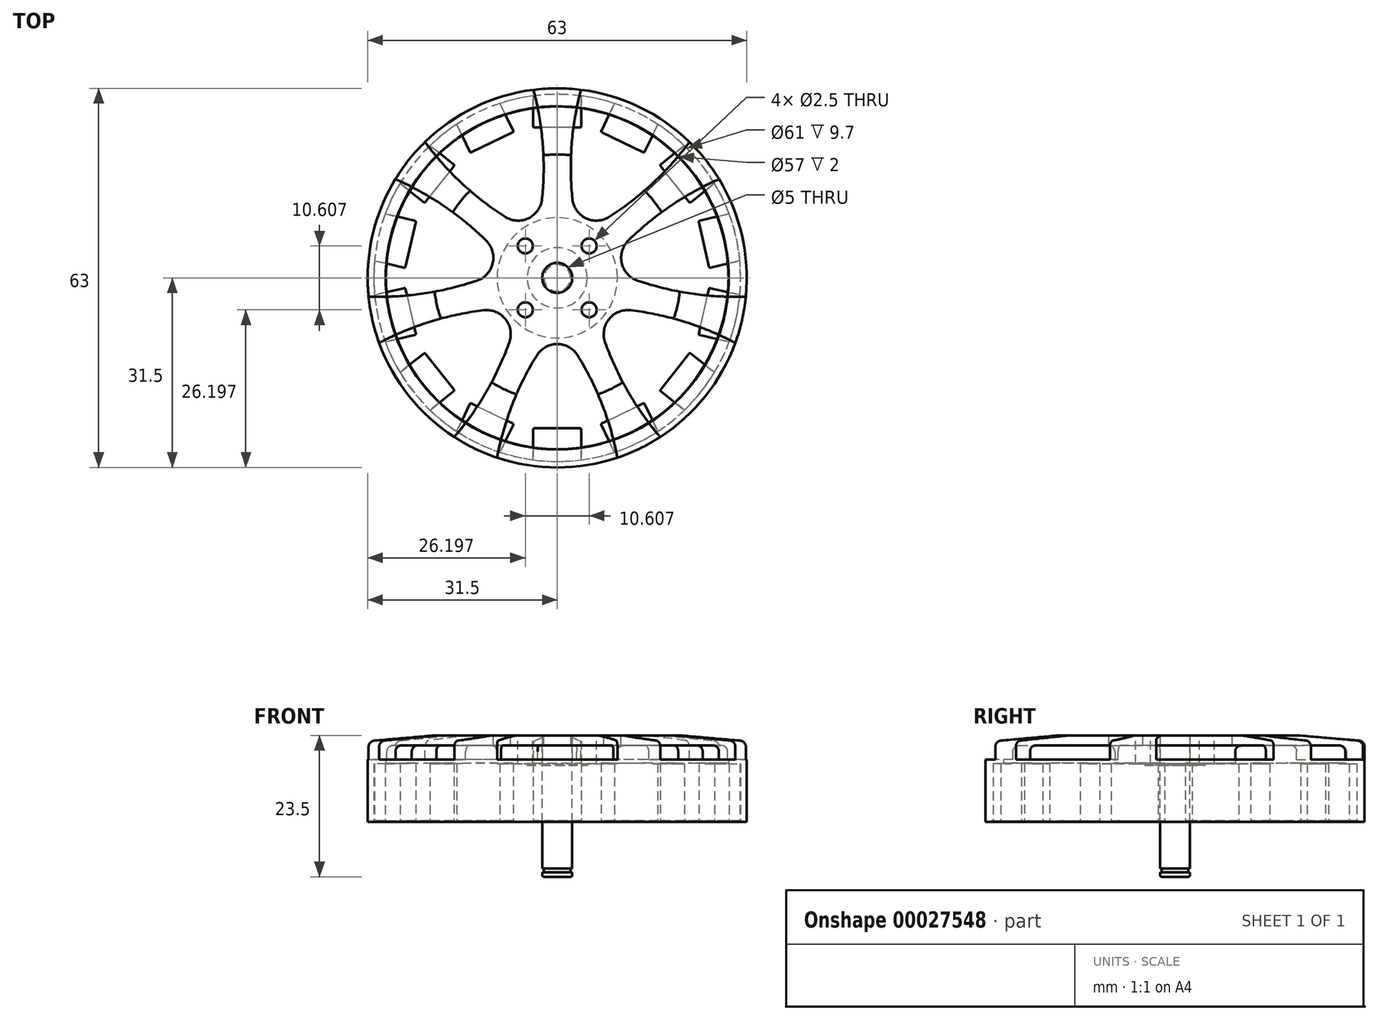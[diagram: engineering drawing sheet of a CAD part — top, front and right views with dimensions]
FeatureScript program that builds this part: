
annotation { "Feature Type Name" : "Feature", "Feature Type Description" : "" }
export const myFeature = defineFeature(function(context is Context, id is Id, definition is map)
    precondition{}
    {
        {
            var Q0;
            Q0=qCreatedBy(makeId("Front.planeOp"),FACE);
            var sketch = newSketch(context, id + "F0", { "sketchPlane" : qUnion([Q0])});
            skLineSegment(sketch, "E0", {"start": v(-2.5, 14.4) * mm, "end": v(-20.5, 14.4) * mm});
            skLineSegment(sketch, "E1", {"start": v(-20.5, 14.4) * mm, "end": v(-30.59, 13.52) * mm});
            skLineSegment(sketch, "E2", {"start": v(-31.5, 12.52) * mm, "end": v(-31.5, 0) * mm});
            skLineSegment(sketch, "E3", {"start": v(-31.5, 0) * mm, "end": v(-30.5, 0) * mm});
            skLineSegment(sketch, "E4", {"start": v(-30.5, 0) * mm, "end": v(-30.5, 9.7) * mm});
            skLineSegment(sketch, "E5", {"start": v(-10, 11.7) * mm, "end": v(-10, 9.7) * mm});
            skLineSegment(sketch, "E6", {"start": v(-10, 9.7) * mm, "end": v(-5, 9.7) * mm});
            skLineSegment(sketch, "E7", {"start": v(-2.5, 14.4) * mm, "end": v(-2.5, 9.7) * mm});
            skLineSegment(sketch, "E8", {"start": v(-30.5, 9.7) * mm, "end": v(-28.5, 9.7) * mm});
            skLineSegment(sketch, "E9", {"start": v(-28.5, 9.7) * mm, "end": v(-28.5, 11.7) * mm});
            skLineSegment(sketch, "E10", {"start": v(-27.5, 12.7) * mm, "end": v(-11, 12.7) * mm});
            skPoint(sketch, "E11.visualSharp", {"position": v(-28.5, 12.7) * mm});
            skArc(sketch, "E11.filletArc", {"start": v(-27.5, 12.7) * mm, "mid": v(-28.2, 12.4) * mm, "end": v(-28.5, 11.7) * mm});
            skPoint(sketch, "E12.visualSharp", {"position": v(-31.5, 13.44) * mm});
            skArc(sketch, "E12.filletArc", {"start": v(-30.59, 13.52) * mm, "mid": v(-31.24, 13.2) * mm, "end": v(-31.5, 12.52) * mm});
            skPoint(sketch, "E13.visualSharp", {"position": v(-10, 12.7) * mm});
            skArc(sketch, "E13.filletArc", {"start": v(-10, 11.7) * mm, "mid": v(-10.3, 12.4) * mm, "end": v(-11, 12.7) * mm});
            skLineSegment(sketch, "E14", {"start": v(0, 0) * mm, "end": v(0, 25.5) * mm, "construction": true});
            skLineSegment(sketch, "E15", {"start": v(-5, 9.7) * mm, "end": v(-5, 9.4) * mm});
            skLineSegment(sketch, "E16", {"start": v(-5, 9.4) * mm, "end": v(-2.5, 9.4) * mm});
            skLineSegment(sketch, "E17", {"start": v(-2.5, 9.4) * mm, "end": v(-2.5, 9.7) * mm});
            skSolve(sketch);
        }
        {
            var Q0;
            Q0=makeQuery(id+"F0.imprint","IMPRINT",FACE,{"disambiguationData":[TD([[makeQuery(id+"F0.imprint","IMPRINT",EDGE,{"derivedFrom":sQuery(id+"F0.wireOp",EDGE,"E0")}),1.0]])]});
            var Q1;
            Q1=sQuery(id+"F0.wireOp",EDGE,"E14");
            revolve(context, id + "F1", {"entities" : qUnion([Q0]), "axis" : qUnion([Q1]), "revolveType" : RevolveType.FULL});
        }
        {
            var Q0;
            Q0=makeQuery(id+"F1.opRevolve","SWEPT_FACE",FACE,{"disambiguationData":[OSD([sQuery(id+"F0.wireOp",EDGE,"E0")])]});
            var sketch = newSketch(context, id + "F2", { "sketchPlane" : qUnion([Q0])});
            skArc(sketch, "E18", {"start": v(0, -11) * mm, "mid": v(-1.95, -11.5) * mm, "end": v(-3.4, -12.9) * mm});
            skArc(sketch, "E19.0", {"start": v(-10, -29.87) * mm, "mid": v(-5.07, -31.09) * mm, "end": v(0, -31.5) * mm});
            skArc(sketch, "E20", {"start": v(-3.4, -12.9) * mm, "mid": v(-7.48, -21.08) * mm, "end": v(-10, -29.87) * mm});
            skLineSegment(sketch, "E21", {"start": v(0, 0) * mm, "end": v(0, -34.41) * mm, "construction": true});
            skPoint(sketch, "E22", {"position": v(0, -11) * mm});
            skPoint(sketch, "E23", {"position": v(0, -31.5) * mm});
            skArc(sketch, "E24.MirrorCS", {"start": v(0, -11) * mm, "mid": v(1.95, -11.5) * mm, "end": v(3.4, -12.9) * mm});
            skArc(sketch, "E25.MirrorCS", {"start": v(10, -29.87) * mm, "mid": v(5.07, -31.09) * mm, "end": v(0, -31.5) * mm});
            skArc(sketch, "E26.MirrorCS", {"start": v(3.4, -12.9) * mm, "mid": v(7.48, -21.08) * mm, "end": v(10, -29.87) * mm});
            skPoint(sketch, "E27.1.0", {"position": v(24.63, -19.64) * mm});
            skPoint(sketch, "E27.1.1", {"position": v(8.6, -6.86) * mm});
            skArc(sketch, "E27.1.2", {"start": v(17.12, -26.44) * mm, "mid": v(21.15, -23.34) * mm, "end": v(24.63, -19.64) * mm});
            skArc(sketch, "E27.1.3", {"start": v(7.96, -10.7) * mm, "mid": v(11.82, -19) * mm, "end": v(17.12, -26.44) * mm});
            skArc(sketch, "E27.1.4", {"start": v(29.59, -10.8) * mm, "mid": v(27.47, -15.42) * mm, "end": v(24.63, -19.64) * mm});
            skArc(sketch, "E27.1.5", {"start": v(12.2, -5.38) * mm, "mid": v(21.15, -7.3) * mm, "end": v(29.59, -10.8) * mm});
            skPoint(sketch, "E27.1.6", {"position": v(24.63, -19.64) * mm});
            skPoint(sketch, "E27.1.7", {"position": v(8.6, -6.86) * mm});
            skArc(sketch, "E27.1.8", {"start": v(8.6, -6.86) * mm, "mid": v(7.78, -8.7) * mm, "end": v(7.96, -10.7) * mm});
            skArc(sketch, "E27.1.9", {"start": v(8.6, -6.86) * mm, "mid": v(10.2, -5.65) * mm, "end": v(12.2, -5.38) * mm});
            skPoint(sketch, "E27.2.0", {"position": v(30.71, 7) * mm});
            skPoint(sketch, "E27.2.1", {"position": v(10.72, 2.45) * mm});
            skArc(sketch, "E27.2.2", {"start": v(31.35, -3.1) * mm, "mid": v(31.44, 1.98) * mm, "end": v(30.71, 7) * mm});
            skArc(sketch, "E27.2.3", {"start": v(13.33, -0.45) * mm, "mid": v(22.22, -2.6) * mm, "end": v(31.35, -3.1) * mm});
            skArc(sketch, "E27.2.4", {"start": v(26.9, 16.4) * mm, "mid": v(29.18, 11.86) * mm, "end": v(30.71, 7) * mm});
            skArc(sketch, "E27.2.5", {"start": v(11.82, 6.19) * mm, "mid": v(18.89, 11.98) * mm, "end": v(26.9, 16.4) * mm});
            skPoint(sketch, "E27.2.6", {"position": v(30.71, 7) * mm});
            skPoint(sketch, "E27.2.7", {"position": v(10.72, 2.45) * mm});
            skArc(sketch, "E27.2.8", {"start": v(10.72, 2.45) * mm, "mid": v(11.65, 0.66) * mm, "end": v(13.33, -0.45) * mm});
            skArc(sketch, "E27.2.9", {"start": v(10.72, 2.45) * mm, "mid": v(10.78, 4.46) * mm, "end": v(11.82, 6.19) * mm});
            skPoint(sketch, "E27.3.0", {"position": v(13.67, 28.38) * mm});
            skPoint(sketch, "E27.3.1", {"position": v(4.77, 9.91) * mm});
            skArc(sketch, "E27.3.2", {"start": v(21.97, 22.57) * mm, "mid": v(18.05, 25.81) * mm, "end": v(13.67, 28.38) * mm});
            skArc(sketch, "E27.3.3", {"start": v(8.66, 10.14) * mm, "mid": v(15.89, 15.75) * mm, "end": v(21.97, 22.57) * mm});
            skArc(sketch, "E27.3.4", {"start": v(3.95, 31.25) * mm, "mid": v(8.93, 30.2) * mm, "end": v(13.67, 28.38) * mm});
            skArc(sketch, "E27.3.5", {"start": v(2.53, 13.1) * mm, "mid": v(2.4, 22.24) * mm, "end": v(3.95, 31.25) * mm});
            skPoint(sketch, "E27.3.6", {"position": v(13.67, 28.38) * mm});
            skPoint(sketch, "E27.3.7", {"position": v(4.77, 9.91) * mm});
            skArc(sketch, "E27.3.8", {"start": v(4.77, 9.91) * mm, "mid": v(6.75, 9.52) * mm, "end": v(8.66, 10.14) * mm});
            skArc(sketch, "E27.3.9", {"start": v(4.77, 9.91) * mm, "mid": v(3.24, 11.21) * mm, "end": v(2.53, 13.1) * mm});
            skPoint(sketch, "E27.4.0", {"position": v(-13.67, 28.38) * mm});
            skPoint(sketch, "E27.4.1", {"position": v(-4.77, 9.91) * mm});
            skArc(sketch, "E27.4.2", {"start": v(-3.95, 31.25) * mm, "mid": v(-8.93, 30.2) * mm, "end": v(-13.67, 28.38) * mm});
            skArc(sketch, "E27.4.3", {"start": v(-2.53, 13.1) * mm, "mid": v(-2.4, 22.24) * mm, "end": v(-3.95, 31.25) * mm});
            skArc(sketch, "E27.4.4", {"start": v(-21.97, 22.57) * mm, "mid": v(-18.05, 25.81) * mm, "end": v(-13.67, 28.38) * mm});
            skArc(sketch, "E27.4.5", {"start": v(-8.66, 10.14) * mm, "mid": v(-15.89, 15.75) * mm, "end": v(-21.97, 22.57) * mm});
            skPoint(sketch, "E27.4.6", {"position": v(-13.67, 28.38) * mm});
            skPoint(sketch, "E27.4.7", {"position": v(-4.77, 9.91) * mm});
            skArc(sketch, "E27.4.8", {"start": v(-4.77, 9.91) * mm, "mid": v(-3.24, 11.21) * mm, "end": v(-2.53, 13.1) * mm});
            skArc(sketch, "E27.4.9", {"start": v(-4.77, 9.91) * mm, "mid": v(-6.75, 9.52) * mm, "end": v(-8.66, 10.14) * mm});
            skPoint(sketch, "E27.5.0", {"position": v(-30.71, 7) * mm});
            skPoint(sketch, "E27.5.1", {"position": v(-10.72, 2.45) * mm});
            skArc(sketch, "E27.5.2", {"start": v(-26.9, 16.4) * mm, "mid": v(-29.18, 11.86) * mm, "end": v(-30.71, 7) * mm});
            skArc(sketch, "E27.5.3", {"start": v(-11.82, 6.19) * mm, "mid": v(-18.89, 11.98) * mm, "end": v(-26.9, 16.4) * mm});
            skArc(sketch, "E27.5.4", {"start": v(-31.35, -3.1) * mm, "mid": v(-31.44, 1.98) * mm, "end": v(-30.71, 7) * mm});
            skArc(sketch, "E27.5.5", {"start": v(-13.33, -0.45) * mm, "mid": v(-22.22, -2.6) * mm, "end": v(-31.35, -3.1) * mm});
            skPoint(sketch, "E27.5.6", {"position": v(-30.71, 7) * mm});
            skPoint(sketch, "E27.5.7", {"position": v(-10.72, 2.45) * mm});
            skArc(sketch, "E27.5.8", {"start": v(-10.72, 2.45) * mm, "mid": v(-10.78, 4.46) * mm, "end": v(-11.82, 6.19) * mm});
            skArc(sketch, "E27.5.9", {"start": v(-10.72, 2.45) * mm, "mid": v(-11.65, 0.66) * mm, "end": v(-13.33, -0.45) * mm});
            skPoint(sketch, "E27.6.0", {"position": v(-24.63, -19.64) * mm});
            skPoint(sketch, "E27.6.1", {"position": v(-8.6, -6.86) * mm});
            skArc(sketch, "E27.6.2", {"start": v(-29.59, -10.8) * mm, "mid": v(-27.47, -15.42) * mm, "end": v(-24.63, -19.64) * mm});
            skArc(sketch, "E27.6.3", {"start": v(-12.2, -5.38) * mm, "mid": v(-21.15, -7.3) * mm, "end": v(-29.59, -10.8) * mm});
            skArc(sketch, "E27.6.4", {"start": v(-17.12, -26.44) * mm, "mid": v(-21.15, -23.34) * mm, "end": v(-24.63, -19.64) * mm});
            skArc(sketch, "E27.6.5", {"start": v(-7.96, -10.7) * mm, "mid": v(-11.82, -19) * mm, "end": v(-17.12, -26.44) * mm});
            skPoint(sketch, "E27.6.6", {"position": v(-24.63, -19.64) * mm});
            skPoint(sketch, "E27.6.7", {"position": v(-8.6, -6.86) * mm});
            skArc(sketch, "E27.6.8", {"start": v(-8.6, -6.86) * mm, "mid": v(-10.2, -5.65) * mm, "end": v(-12.2, -5.38) * mm});
            skArc(sketch, "E27.6.9", {"start": v(-8.6, -6.86) * mm, "mid": v(-7.78, -8.7) * mm, "end": v(-7.96, -10.7) * mm});
            skSolve(sketch);
        }
        {
            var Q0;
            Q0 = qSketchRegion(id + "F2", true);
            extrude(context, id + "F3", {"entities" : qUnion([Q0]), "operationType" : NewBodyOperationType.REMOVE, "oppositeDirection" : true, "depth" : 4 * mm});
        }
        {
            var Q0;
            Q0=makeQuery(id+"F1.opRevolve","SWEPT_FACE",FACE,{"disambiguationData":[OSD([sQuery(id+"F0.wireOp",EDGE,"E0")])]});
            var sketch = newSketch(context, id + "F4", { "sketchPlane" : qUnion([Q0])});
            skCircle(sketch, "E28", {"center": v(5.3, 5.3) * mm, "radius": 1.25 * mm});
            skLineSegment(sketch, "E29", {"start": v(0, 0) * mm, "end": v(5.3, 5.3) * mm, "construction": true});
            skLineSegment(sketch, "E30", {"start": v(0, 0) * mm, "end": v(9.9, 0) * mm, "construction": true});
            skCircle(sketch, "E31.1.0", {"center": v(-5.3, 5.3) * mm, "radius": 1.25 * mm});
            skCircle(sketch, "E31.2.0", {"center": v(-5.3, -5.3) * mm, "radius": 1.25 * mm});
            skPoint(sketch, "E31.center", {"position": v(0, 0) * mm});
            skCircle(sketch, "E32.1.3.0", {"center": v(5.3, -5.3) * mm, "radius": 1.25 * mm});
            skSolve(sketch);
        }
        {
            var Q0;
            Q0 = qSketchRegion(id + "F4", true);
            var Q1;
            Q1=makeQuery(id+"F1.opRevolve","SWEPT_FACE",FACE,{"disambiguationData":[OSD([sQuery(id+"F0.wireOp",EDGE,"E6")])]});
            extrude(context, id + "F5", {"entities" : qUnion([Q0]), "operationType" : NewBodyOperationType.REMOVE, "endBound" : BoundingType.UP_TO_SURFACE, "oppositeDirection" : true, "endBoundEntityFace" : qUnion([Q1]), "depth" : 25.4 * mm});
        }
        {
            var Q0;
            Q0=qCreatedBy(makeId("Top.planeOp"),FACE);
            cPlane(context, id + "F6", {"entities" : qUnion([Q0]), "cplaneType" : CPlaneType.OFFSET, "offset" : .2 * mm, "width" : 152.4 * mm, "height" : 152.4 * mm});
        }
        {
            var Q0;
            Q0=qCreatedBy(id+"F6.planeOp",FACE);
            var sketch = newSketch(context, id + "F7", { "sketchPlane" : qUnion([Q0])});
            skArc(sketch, "E33.1", {"start": v(-4, -30.24) * mm, "mid": v(0, -30.5) * mm, "end": v(4, -30.24) * mm});
            skLineSegment(sketch, "E34", {"start": v(0, -33.5) * mm, "end": v(0, -24.9) * mm, "construction": true});
            skLineSegment(sketch, "E35.0", {"start": v(4, -30.24) * mm, "end": v(4, -25.2) * mm});
            skLineSegment(sketch, "E36.0", {"start": v(-4, -30.24) * mm, "end": v(-4, -25.2) * mm});
            skLineSegment(sketch, "E37", {"start": v(-3.8, -25) * mm, "end": v(3.8, -25) * mm});
            skPoint(sketch, "E38.visualSharp", {"position": v(-4, -25) * mm});
            skArc(sketch, "E38.filletArc", {"start": v(-3.8, -25) * mm, "mid": v(-3.94, -25.06) * mm, "end": v(-4, -25.2) * mm});
            skPoint(sketch, "E39.visualSharp", {"position": v(4, -25) * mm});
            skArc(sketch, "E39.filletArc", {"start": v(4, -25.2) * mm, "mid": v(3.94, -25.06) * mm, "end": v(3.8, -25) * mm});
            skPoint(sketch, "E40.1.0", {"position": v(7.24, -24.26) * mm});
            skArc(sketch, "E40.1.1", {"start": v(9.52, -28.98) * mm, "mid": v(13.23, -27.48) * mm, "end": v(16.72, -25.5) * mm});
            skLineSegment(sketch, "E40.1.2", {"start": v(7.42, -24.17) * mm, "end": v(14.27, -20.88) * mm});
            skLineSegment(sketch, "E40.1.3", {"start": v(16.72, -25.5) * mm, "end": v(14.54, -20.97) * mm});
            skLineSegment(sketch, "E40.1.4", {"start": v(9.52, -28.98) * mm, "end": v(7.33, -24.44) * mm});
            skPoint(sketch, "E40.1.5", {"position": v(14.45, -20.79) * mm});
            skArc(sketch, "E40.1.6", {"start": v(14.54, -20.97) * mm, "mid": v(14.42, -20.87) * mm, "end": v(14.27, -20.88) * mm});
            skArc(sketch, "E40.1.7", {"start": v(7.42, -24.17) * mm, "mid": v(7.32, -24.29) * mm, "end": v(7.33, -24.44) * mm});
            skPoint(sketch, "E40.2.0", {"position": v(17.05, -18.71) * mm});
            skArc(sketch, "E40.2.1", {"start": v(21.15, -21.98) * mm, "mid": v(23.85, -19.02) * mm, "end": v(26.13, -15.72) * mm});
            skLineSegment(sketch, "E40.2.2", {"start": v(17.18, -18.56) * mm, "end": v(21.92, -12.62) * mm});
            skLineSegment(sketch, "E40.2.3", {"start": v(26.13, -15.72) * mm, "end": v(22.2, -12.58) * mm});
            skLineSegment(sketch, "E40.2.4", {"start": v(21.15, -21.98) * mm, "end": v(17.2, -18.84) * mm});
            skPoint(sketch, "E40.2.5", {"position": v(22.04, -12.46) * mm});
            skArc(sketch, "E40.2.6", {"start": v(22.2, -12.58) * mm, "mid": v(22.05, -12.54) * mm, "end": v(21.92, -12.62) * mm});
            skArc(sketch, "E40.2.7", {"start": v(17.18, -18.56) * mm, "mid": v(17.13, -18.7) * mm, "end": v(17.2, -18.84) * mm});
            skPoint(sketch, "E41.0.3.0", {"position": v(23.48, -9.46) * mm});
            skArc(sketch, "E41.1.3.0", {"start": v(28.59, -10.63) * mm, "mid": v(29.74, -6.79) * mm, "end": v(30.37, -2.83) * mm});
            skLineSegment(sketch, "E41.5.3.0", {"start": v(23.53, -9.27) * mm, "end": v(25.22, -1.86) * mm});
            skLineSegment(sketch, "E41.8.3.0", {"start": v(30.37, -2.83) * mm, "end": v(25.46, -1.7) * mm});
            skLineSegment(sketch, "E41.11.3.0", {"start": v(28.59, -10.63) * mm, "end": v(23.68, -9.5) * mm});
            skPoint(sketch, "E41.14.3.0", {"position": v(25.26, -1.66) * mm});
            skArc(sketch, "E41.15.3.0", {"start": v(25.46, -1.7) * mm, "mid": v(25.3, -1.73) * mm, "end": v(25.22, -1.86) * mm});
            skArc(sketch, "E41.19.3.0", {"start": v(23.53, -9.27) * mm, "mid": v(23.55, -9.42) * mm, "end": v(23.68, -9.5) * mm});
            skPoint(sketch, "E41.0.4.0", {"position": v(25.26, 1.66) * mm});
            skArc(sketch, "E41.1.4.0", {"start": v(30.37, 2.83) * mm, "mid": v(29.74, 6.79) * mm, "end": v(28.59, 10.63) * mm});
            skLineSegment(sketch, "E41.5.4.0", {"start": v(25.22, 1.86) * mm, "end": v(23.53, 9.27) * mm});
            skLineSegment(sketch, "E41.8.4.0", {"start": v(28.59, 10.63) * mm, "end": v(23.68, 9.5) * mm});
            skLineSegment(sketch, "E41.11.4.0", {"start": v(30.37, 2.83) * mm, "end": v(25.46, 1.7) * mm});
            skPoint(sketch, "E41.14.4.0", {"position": v(23.48, 9.46) * mm});
            skArc(sketch, "E41.15.4.0", {"start": v(23.68, 9.5) * mm, "mid": v(23.55, 9.42) * mm, "end": v(23.53, 9.27) * mm});
            skArc(sketch, "E41.19.4.0", {"start": v(25.22, 1.86) * mm, "mid": v(25.3, 1.73) * mm, "end": v(25.46, 1.7) * mm});
            skPoint(sketch, "E41.0.5.0", {"position": v(22.04, 12.46) * mm});
            skArc(sketch, "E41.1.5.0", {"start": v(26.13, 15.72) * mm, "mid": v(23.85, 19.02) * mm, "end": v(21.15, 21.98) * mm});
            skLineSegment(sketch, "E41.5.5.0", {"start": v(21.92, 12.62) * mm, "end": v(17.18, 18.56) * mm});
            skLineSegment(sketch, "E41.8.5.0", {"start": v(21.15, 21.98) * mm, "end": v(17.2, 18.84) * mm});
            skLineSegment(sketch, "E41.11.5.0", {"start": v(26.13, 15.72) * mm, "end": v(22.2, 12.58) * mm});
            skPoint(sketch, "E41.14.5.0", {"position": v(17.05, 18.71) * mm});
            skArc(sketch, "E41.15.5.0", {"start": v(17.2, 18.84) * mm, "mid": v(17.13, 18.7) * mm, "end": v(17.18, 18.56) * mm});
            skArc(sketch, "E41.19.5.0", {"start": v(21.92, 12.62) * mm, "mid": v(22.05, 12.54) * mm, "end": v(22.2, 12.58) * mm});
            skPoint(sketch, "E41.0.6.0", {"position": v(14.45, 20.79) * mm});
            skArc(sketch, "E41.1.6.0", {"start": v(16.72, 25.5) * mm, "mid": v(13.23, 27.48) * mm, "end": v(9.52, 28.98) * mm});
            skLineSegment(sketch, "E41.5.6.0", {"start": v(14.27, 20.88) * mm, "end": v(7.42, 24.17) * mm});
            skLineSegment(sketch, "E41.8.6.0", {"start": v(9.52, 28.98) * mm, "end": v(7.33, 24.44) * mm});
            skLineSegment(sketch, "E41.11.6.0", {"start": v(16.72, 25.5) * mm, "end": v(14.54, 20.97) * mm});
            skPoint(sketch, "E41.14.6.0", {"position": v(7.24, 24.26) * mm});
            skArc(sketch, "E41.15.6.0", {"start": v(7.33, 24.44) * mm, "mid": v(7.32, 24.29) * mm, "end": v(7.42, 24.17) * mm});
            skArc(sketch, "E41.19.6.0", {"start": v(14.27, 20.88) * mm, "mid": v(14.42, 20.87) * mm, "end": v(14.54, 20.97) * mm});
            skPoint(sketch, "E41.0.7.0", {"position": v(4, 25) * mm});
            skArc(sketch, "E41.1.7.0", {"start": v(4, 30.24) * mm, "mid": v(0, 30.5) * mm, "end": v(-4, 30.24) * mm});
            skLineSegment(sketch, "E41.5.7.0", {"start": v(3.8, 25) * mm, "end": v(-3.8, 25) * mm});
            skLineSegment(sketch, "E41.8.7.0", {"start": v(-4, 30.24) * mm, "end": v(-4, 25.2) * mm});
            skLineSegment(sketch, "E41.11.7.0", {"start": v(4, 30.24) * mm, "end": v(4, 25.2) * mm});
            skPoint(sketch, "E41.14.7.0", {"position": v(-4, 25) * mm});
            skArc(sketch, "E41.15.7.0", {"start": v(-4, 25.2) * mm, "mid": v(-3.94, 25.06) * mm, "end": v(-3.8, 25) * mm});
            skArc(sketch, "E41.19.7.0", {"start": v(3.8, 25) * mm, "mid": v(3.94, 25.06) * mm, "end": v(4, 25.2) * mm});
            skPoint(sketch, "E41.0.8.0", {"position": v(-7.24, 24.26) * mm});
            skArc(sketch, "E41.1.8.0", {"start": v(-9.52, 28.98) * mm, "mid": v(-13.23, 27.48) * mm, "end": v(-16.72, 25.5) * mm});
            skLineSegment(sketch, "E41.5.8.0", {"start": v(-7.42, 24.17) * mm, "end": v(-14.27, 20.88) * mm});
            skLineSegment(sketch, "E41.8.8.0", {"start": v(-16.72, 25.5) * mm, "end": v(-14.54, 20.97) * mm});
            skLineSegment(sketch, "E41.11.8.0", {"start": v(-9.52, 28.98) * mm, "end": v(-7.33, 24.44) * mm});
            skPoint(sketch, "E41.14.8.0", {"position": v(-14.45, 20.79) * mm});
            skArc(sketch, "E41.15.8.0", {"start": v(-14.54, 20.97) * mm, "mid": v(-14.42, 20.87) * mm, "end": v(-14.27, 20.88) * mm});
            skArc(sketch, "E41.19.8.0", {"start": v(-7.42, 24.17) * mm, "mid": v(-7.32, 24.29) * mm, "end": v(-7.33, 24.44) * mm});
            skPoint(sketch, "E41.0.9.0", {"position": v(-17.05, 18.71) * mm});
            skArc(sketch, "E41.1.9.0", {"start": v(-21.15, 21.98) * mm, "mid": v(-23.85, 19.02) * mm, "end": v(-26.13, 15.72) * mm});
            skLineSegment(sketch, "E41.5.9.0", {"start": v(-17.18, 18.56) * mm, "end": v(-21.92, 12.62) * mm});
            skLineSegment(sketch, "E41.8.9.0", {"start": v(-26.13, 15.72) * mm, "end": v(-22.2, 12.58) * mm});
            skLineSegment(sketch, "E41.11.9.0", {"start": v(-21.15, 21.98) * mm, "end": v(-17.2, 18.84) * mm});
            skPoint(sketch, "E41.14.9.0", {"position": v(-22.04, 12.46) * mm});
            skArc(sketch, "E41.15.9.0", {"start": v(-22.2, 12.58) * mm, "mid": v(-22.05, 12.54) * mm, "end": v(-21.92, 12.62) * mm});
            skArc(sketch, "E41.19.9.0", {"start": v(-17.18, 18.56) * mm, "mid": v(-17.13, 18.7) * mm, "end": v(-17.2, 18.84) * mm});
            skPoint(sketch, "E41.0.10.0", {"position": v(-23.48, 9.46) * mm});
            skArc(sketch, "E41.1.10.0", {"start": v(-28.59, 10.63) * mm, "mid": v(-29.74, 6.79) * mm, "end": v(-30.37, 2.83) * mm});
            skLineSegment(sketch, "E41.5.10.0", {"start": v(-23.53, 9.27) * mm, "end": v(-25.22, 1.86) * mm});
            skLineSegment(sketch, "E41.8.10.0", {"start": v(-30.37, 2.83) * mm, "end": v(-25.46, 1.7) * mm});
            skLineSegment(sketch, "E41.11.10.0", {"start": v(-28.59, 10.63) * mm, "end": v(-23.68, 9.5) * mm});
            skPoint(sketch, "E41.14.10.0", {"position": v(-25.26, 1.66) * mm});
            skArc(sketch, "E41.15.10.0", {"start": v(-25.46, 1.7) * mm, "mid": v(-25.3, 1.73) * mm, "end": v(-25.22, 1.86) * mm});
            skArc(sketch, "E41.19.10.0", {"start": v(-23.53, 9.27) * mm, "mid": v(-23.55, 9.42) * mm, "end": v(-23.68, 9.5) * mm});
            skPoint(sketch, "E41.0.11.0", {"position": v(-25.26, -1.66) * mm});
            skArc(sketch, "E41.1.11.0", {"start": v(-30.37, -2.83) * mm, "mid": v(-29.74, -6.79) * mm, "end": v(-28.59, -10.63) * mm});
            skLineSegment(sketch, "E41.5.11.0", {"start": v(-25.22, -1.86) * mm, "end": v(-23.53, -9.27) * mm});
            skLineSegment(sketch, "E41.8.11.0", {"start": v(-28.59, -10.63) * mm, "end": v(-23.68, -9.5) * mm});
            skLineSegment(sketch, "E41.11.11.0", {"start": v(-30.37, -2.83) * mm, "end": v(-25.46, -1.7) * mm});
            skPoint(sketch, "E41.14.11.0", {"position": v(-23.48, -9.46) * mm});
            skArc(sketch, "E41.15.11.0", {"start": v(-23.68, -9.5) * mm, "mid": v(-23.55, -9.42) * mm, "end": v(-23.53, -9.27) * mm});
            skArc(sketch, "E41.19.11.0", {"start": v(-25.22, -1.86) * mm, "mid": v(-25.3, -1.73) * mm, "end": v(-25.46, -1.7) * mm});
            skPoint(sketch, "E41.0.12.0", {"position": v(-22.04, -12.46) * mm});
            skArc(sketch, "E41.1.12.0", {"start": v(-26.13, -15.72) * mm, "mid": v(-23.85, -19.02) * mm, "end": v(-21.15, -21.98) * mm});
            skLineSegment(sketch, "E41.5.12.0", {"start": v(-21.92, -12.62) * mm, "end": v(-17.18, -18.56) * mm});
            skLineSegment(sketch, "E41.8.12.0", {"start": v(-21.15, -21.98) * mm, "end": v(-17.2, -18.84) * mm});
            skLineSegment(sketch, "E41.11.12.0", {"start": v(-26.13, -15.72) * mm, "end": v(-22.2, -12.58) * mm});
            skPoint(sketch, "E41.14.12.0", {"position": v(-17.05, -18.71) * mm});
            skArc(sketch, "E41.15.12.0", {"start": v(-17.2, -18.84) * mm, "mid": v(-17.13, -18.7) * mm, "end": v(-17.18, -18.56) * mm});
            skArc(sketch, "E41.19.12.0", {"start": v(-21.92, -12.62) * mm, "mid": v(-22.05, -12.54) * mm, "end": v(-22.2, -12.58) * mm});
            skPoint(sketch, "E41.0.13.0", {"position": v(-14.45, -20.79) * mm});
            skArc(sketch, "E41.1.13.0", {"start": v(-16.72, -25.5) * mm, "mid": v(-13.23, -27.48) * mm, "end": v(-9.52, -28.98) * mm});
            skLineSegment(sketch, "E41.5.13.0", {"start": v(-14.27, -20.88) * mm, "end": v(-7.42, -24.17) * mm});
            skLineSegment(sketch, "E41.8.13.0", {"start": v(-9.52, -28.98) * mm, "end": v(-7.33, -24.44) * mm});
            skLineSegment(sketch, "E41.11.13.0", {"start": v(-16.72, -25.5) * mm, "end": v(-14.54, -20.97) * mm});
            skPoint(sketch, "E41.14.13.0", {"position": v(-7.24, -24.26) * mm});
            skArc(sketch, "E41.15.13.0", {"start": v(-7.33, -24.44) * mm, "mid": v(-7.32, -24.29) * mm, "end": v(-7.42, -24.17) * mm});
            skArc(sketch, "E41.19.13.0", {"start": v(-14.27, -20.88) * mm, "mid": v(-14.42, -20.87) * mm, "end": v(-14.54, -20.97) * mm});
            skSolve(sketch);
        }
        {
            var Q0;
            Q0 = qSketchRegion(id + "F7", true);
            extrude(context, id + "F8", {"entities" : qUnion([Q0]), "operationType" : NewBodyOperationType.ADD, "depth" : 9.6 * mm});
        }
        {
            var Q0;
            Q0=makeQuery(id+"F1.opRevolve","SWEPT_FACE",FACE,{"disambiguationData":[OSD([sQuery(id+"F0.wireOp",EDGE,"E0")])]});
            var sketch = newSketch(context, id + "F9", { "sketchPlane" : qUnion([Q0])});
            skCircle(sketch, "E42.0", {"center": v(0, 0) * mm, "radius": 2.5 * mm});
            skSolve(sketch);
        }
        {
            var Q0;
            Q0 = qSketchRegion(id + "F9", true);
            extrude(context, id + "F10", {"entities" : qUnion([Q0]), "oppositeDirection" : true, "depth" : 23.5 * mm});
        }
        {
            var Q0;
            Q0=makeQuery(id+"F10.opExtrude","CAP_FACE",FACE,{"disambiguationData":[OSD([sQuery(id+"F9.wireOp",EDGE,"E42.0")])],"isStart":true});
            var Q1;
            Q1=makeQuery(id+"F10.opExtrude","CAP_FACE",FACE,{"disambiguationData":[OSD([sQuery(id+"F9.wireOp",EDGE,"E42.0")])],"isStart":false});
            fillet(context, id + "F11", {"entities" : qUnion([Q0, Q1]), "radius" : .3 * mm, "tangentPropagation" : true, "allowEdgeOverflow" : false});
        }
        {
            var Q0;
            Q0=qCreatedBy(makeId("Front.planeOp"),FACE);
            var sketch = newSketch(context, id + "F12", { "sketchPlane" : qUnion([Q0])});
            skLineSegment(sketch, "E43.bottom", {"start": v(-3.34, -8.35) * mm, "end": v(-2.2, -8.35) * mm});
            skLineSegment(sketch, "E43.top", {"start": v(-3.34, -7.75) * mm, "end": v(-2.2, -7.75) * mm});
            skLineSegment(sketch, "E43.left", {"start": v(-3.34, -8.35) * mm, "end": v(-3.34, -7.75) * mm});
            skLineSegment(sketch, "E43.right", {"start": v(-2.2, -8.35) * mm, "end": v(-2.2, -7.75) * mm});
            skLineSegment(sketch, "E44", {"start": v(0, 0) * mm, "end": v(0, -12.46) * mm, "construction": true});
            skSolve(sketch);
        }
        {
            var Q0;
            Q0 = qSketchRegion(id + "F12", true);
            var Q1;
            Q1=sQuery(id+"F12.wireOp",EDGE,"E44");
            revolve(context, id + "F13", {"operationType" : NewBodyOperationType.REMOVE, "entities" : qUnion([Q0]), "axis" : qUnion([Q1]), "revolveType" : RevolveType.FULL, "oppositeDirection" : true});
        }
    });
